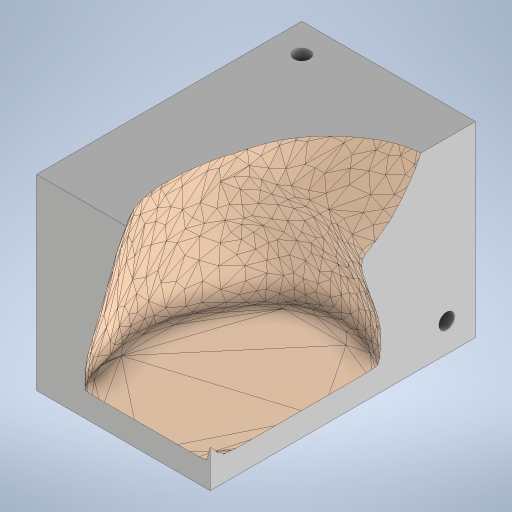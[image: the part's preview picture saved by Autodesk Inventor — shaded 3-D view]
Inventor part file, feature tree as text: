
AUTODESK INVENTOR PART (.ipt)
format: ipt  version: 2024 (Build 280153000, 153)  size: 10,817,024 bytes
history: native  units: mm
features: other x6, sketch x6, extrude x5, plane x2
ambient origin geometry x8: Origin, YZ Plane, XZ Plane, XY Plane, X Axis, Y Axis, Z Axis, Center Point
bodies: Body1 (feature_tree)
feature tree (19):
  other  "M.ipt"
  plane  "Plano de trabajo1"
  extrude  "Extrusión1"  [1 undecoded]
  other  "Combinar1"
  sketch  "Boceto3"  dims[d2=550.0mm d3=520.0mm]
  sketch  "Boceto4"  dims[d4=550.0mm d5=0.0mm d6=129.8482mm]
  plane  "Plano de trabajo2"
  sketch  "Boceto5"  dims[d17=180.0mm d18=180.0mm]
  extrude  "Extrusión2"  Depth=520.0mm
  extrude  "Extrusión3"  Depth=129.8482mm
  extrude  "Extrusión4"  Depth=180.0mm
  extrude  "Extrusión5"  Depth=180.0mm
  other  "Sólido1::M.ipt"
  other  "OperaciónIdentificador1"
  sketch  "Boceto1"  dims[d0=25.0mm d1=-365.0mm]
  other  "Sólido2"
  sketch  "Boceto6"  dims[d22=326.0mm d23=180.0mm]
  sketch  "Boceto7"  dims[d24=180.0mm d25=180.0mm d26=10.0mm d27=0.0mm d28=10.0mm d29=0.0mm d30=30.0mm d31=30.0mm d32=16.0mm d33=16.0mm d34=0.0mm d35=30.0mm d36=30.0mm d37=16.0mm d38=16.0mm d39=0.0mm d14=0.5mm d15=0.872665mm d16=0.5mm d19=0.5mm d20=0.872665mm d21=0.5mm]
  other  "Sólido1"
note: 1 required parameter value undecoded (feature->parameter linkage not recoverable at this tier; creation-order binding heuristic only, values carry confidence <= 0.55)
